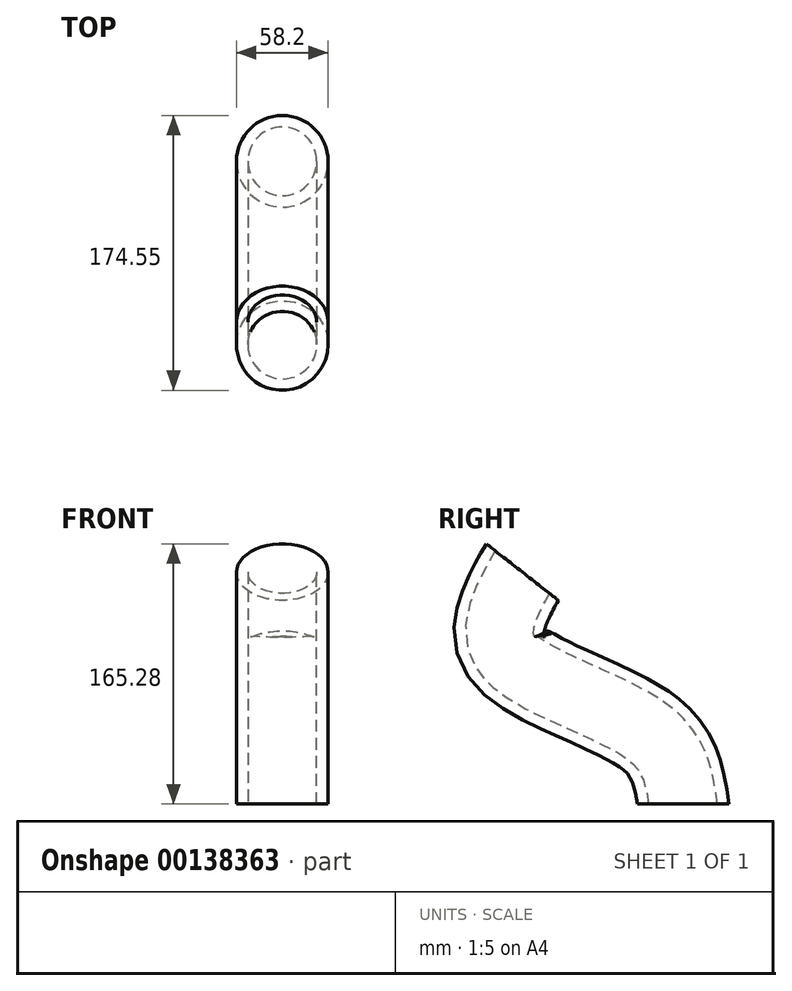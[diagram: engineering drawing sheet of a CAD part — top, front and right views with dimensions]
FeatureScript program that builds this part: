
annotation { "Feature Type Name" : "Feature", "Feature Type Description" : "" }
export const myFeature = defineFeature(function(context is Context, id is Id, definition is map)
    precondition{}
    {
        {
            var Q0;
            Q0=qCreatedBy(makeId("Top.planeOp"),FACE);
            var sketch = newSketch(context, id + "F0", { "sketchPlane" : qUnion([Q0])});
            skCircle(sketch, "E0", {"center": v(0, 0) * mm, "radius": 29.1 * mm});
            skCircle(sketch, "E1", {"center": v(0, 0) * mm, "radius": 21.87 * mm});
            skSolve(sketch);
        }
        {
            var Q0;
            Q0=qCreatedBy(makeId("Right.planeOp"),FACE);
            var sketch = newSketch(context, id + "F1", { "sketchPlane" : qUnion([Q0])});
            skFitSpline(sketch, "E2", {"points": [v(0, 0) * mm, v(-21.36, 44.75) * mm, v(-112.73, 97.34) * mm, v(-102.14, 147.33) * mm], "startDerivative": vector(-25.55, 165.14) * mm, "endDerivative": vector(102.9, 183.32) * mm});
            skSolve(sketch);
        }
        {
            var Q0;
            Q0 = qSketchRegion(id + "F0", true);
            var Q1;
            Q1 = qConstructionFilter(qBodyType(qCreatedBy(id + "F1" ,EDGE), BodyType.WIRE), ConstructionObject.NO);
            sweep(context, id + "F2", {"profiles" : qUnion([Q0]), "path" : qUnion([Q1])});
        }
    });
